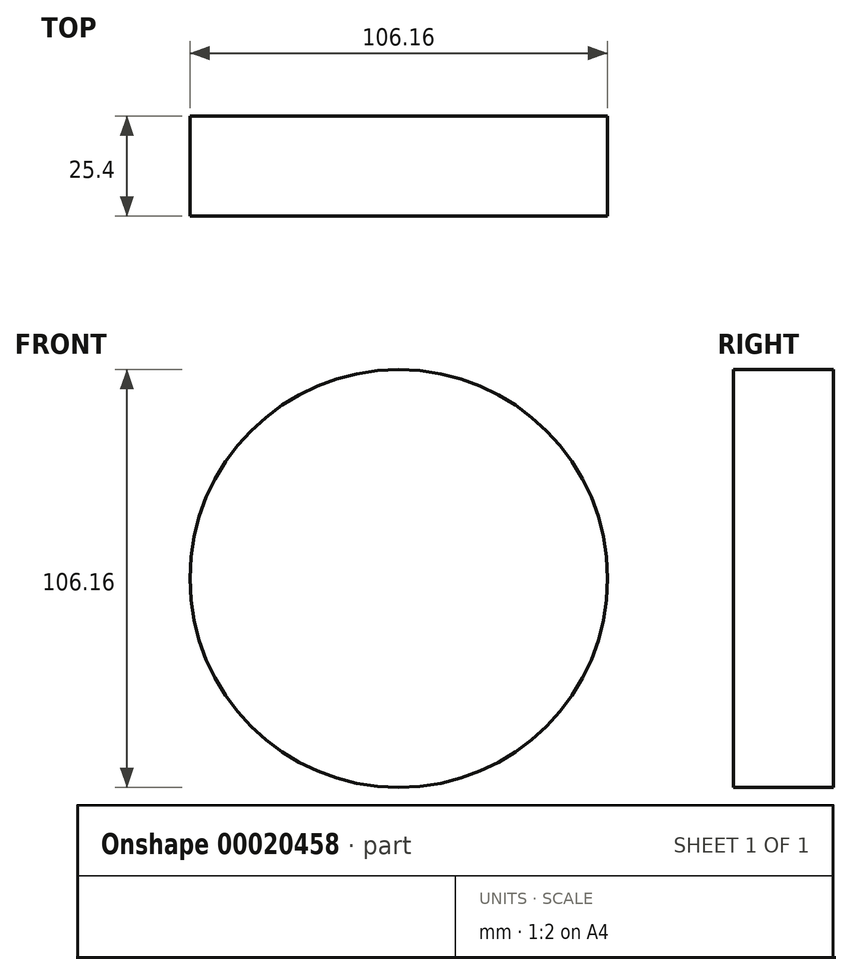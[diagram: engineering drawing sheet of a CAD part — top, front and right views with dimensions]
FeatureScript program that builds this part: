
annotation { "Feature Type Name" : "Feature", "Feature Type Description" : "" }
export const myFeature = defineFeature(function(context is Context, id is Id, definition is map)
    precondition{}
    {
        {
            var Q0;
            Q0=qCreatedBy(makeId("Front.planeOp"),FACE);
            var sketch = newSketch(context, id + "F0", { "sketchPlane" : qUnion([Q0])});
            skCircle(sketch, "E0", {"center": v(0, 0) * mm, "radius": 53.08 * mm});
            skSolve(sketch);
        }
        {
            var Q0;
            Q0=makeQuery(id+"F0.imprint","IMPRINT",FACE,{"disambiguationData":[TD([[makeQuery(id+"F0.imprint","IMPRINT",EDGE,{"derivedFrom":sQuery(id+"F0.wireOp",EDGE,"E0")}),1.0]])]});
            extrude(context, id + "F1", {"entities" : qUnion([Q0]), "depth" : 25.4 * mm});
        }
    });
